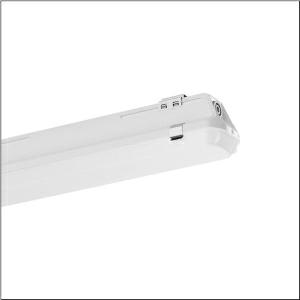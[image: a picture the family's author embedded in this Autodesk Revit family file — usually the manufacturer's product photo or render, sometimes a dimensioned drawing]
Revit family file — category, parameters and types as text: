
# Revit family: monsun_r__11_51fp107p4b0q_de25
name_source: partatom
category: Lighting Fixtures
units: mm (PartAtom-declared; Revit-internal decimal feet)

## family parameters
Cut with Voids When Loaded = No
Host = Face
Light Source = No
Part Type = Normal
Room Calculation Point = No
Round Connector Dimension = Use Diameter
Shared = No

## types (1)
- Monsun® 11 (1 x LED, 12070 lm, 66.2 W, 4000K)
    Apparent Load = 66 VA
    CIE Flux Codes = 47 76 93 94 100
    Color Rendering = 80
    Color Temperature = 4000K
    Default Elevation = 1800 mm
    Description = Monsun® 11, damp-proof luminaire, chain hanger, primary optical cover: enclosure, of PMMA, light emission: direct distribution, primary light characteristic: symmetric, installation type: suspended mounting, surface-mounted, horizontal mounting, vertical mounting, LED, rated luminous flux: 12.070lm, luminous efficacy: 182lm/W, light colour: 840, colour temperature: 4000K, control gear: ECG, with terminal, 3-pole, max. 2.5mm², mains connection: 220..240V, AC, 50/60Hz, rated input power: 66W, luminaire housing, of glass-fibre reinforced polyester, uncoated, bright grey, incl. chain hanger, length: 1.590mm, width: 90mm, height: 88mm, clip for enclosure, of stainless steel (V2A), ceiling mounting element, of stainless steel (V2A), chain hanger, of stainless steel (V2A), protection rating (complete): IP66, insulation class (complete): insulation class I (protective earthing), certification: CE, ENEC, VDE, UKCA, protection symbol: D, impact resistance: IK04, permissible operating ambient temperature: -35..+35°C, standard: EN 50419, EN 60598-2-1, no direct snow, no direct sun, no direct rain, for indoor or canopied outdoor use, corresponds to IFS (International Featured Standards) requirements for safety and quality in the food industry, contact your sales advisor before using the luminaires in applications with unclear chemical exposure, large temperature fluctuations or condensation-forming humidity, LABS conformity tested according to VDMA 24364:2018-05, packaging unit: 1 piece
    Height = 89 mm
    Lamp = 1 x LED
    Lamp Light Flux = 12070 lm
    Lamp Power = 66.2 W
    Lamp count = 1
    Length = 1590 mm
    Luminous efficacy = 182 lm/W
    Manufacturer = Siteco
    ModVariant = No
    Model = 51FP107P4B0Q
    Mounting Place = Ceiling
    Mounting Type = Surface mounted
    Number of Poles = 1
    OnlyDefault = Yes
    Power Factor = 1
    Product Name = Monsun® 11
    Product group = damp-proof luminaire
    ProductGroupID = 300
    Protection Class = Protection class I
    Protection Degree = IP 66
    RLX_Detail_Level = 1
    RLX_Emergency_Light_Flux = 0 lm
    RLX_Emergency_Type = 0
    RLX_Emergency_Type_DB = No
    RlxData = <blob elided: 88769 chars, md5=a8784f0f>
    Socket = socket
    Standby Power = 0 W
    System Light Flux = 12070 lm
    System Power = 66 W
    Type Comments = Product without accessories
    Type Image = l_1004748.jpg
    URL = http://relux.com
    VarID = ---
    Voltage = 0 V
    Weight = 0.00 kg
    Width = 90 mm

## geometry (parser evidence)
native form markers: Blend x4, Sweep x13
no freeform markers — native parametric forms only
